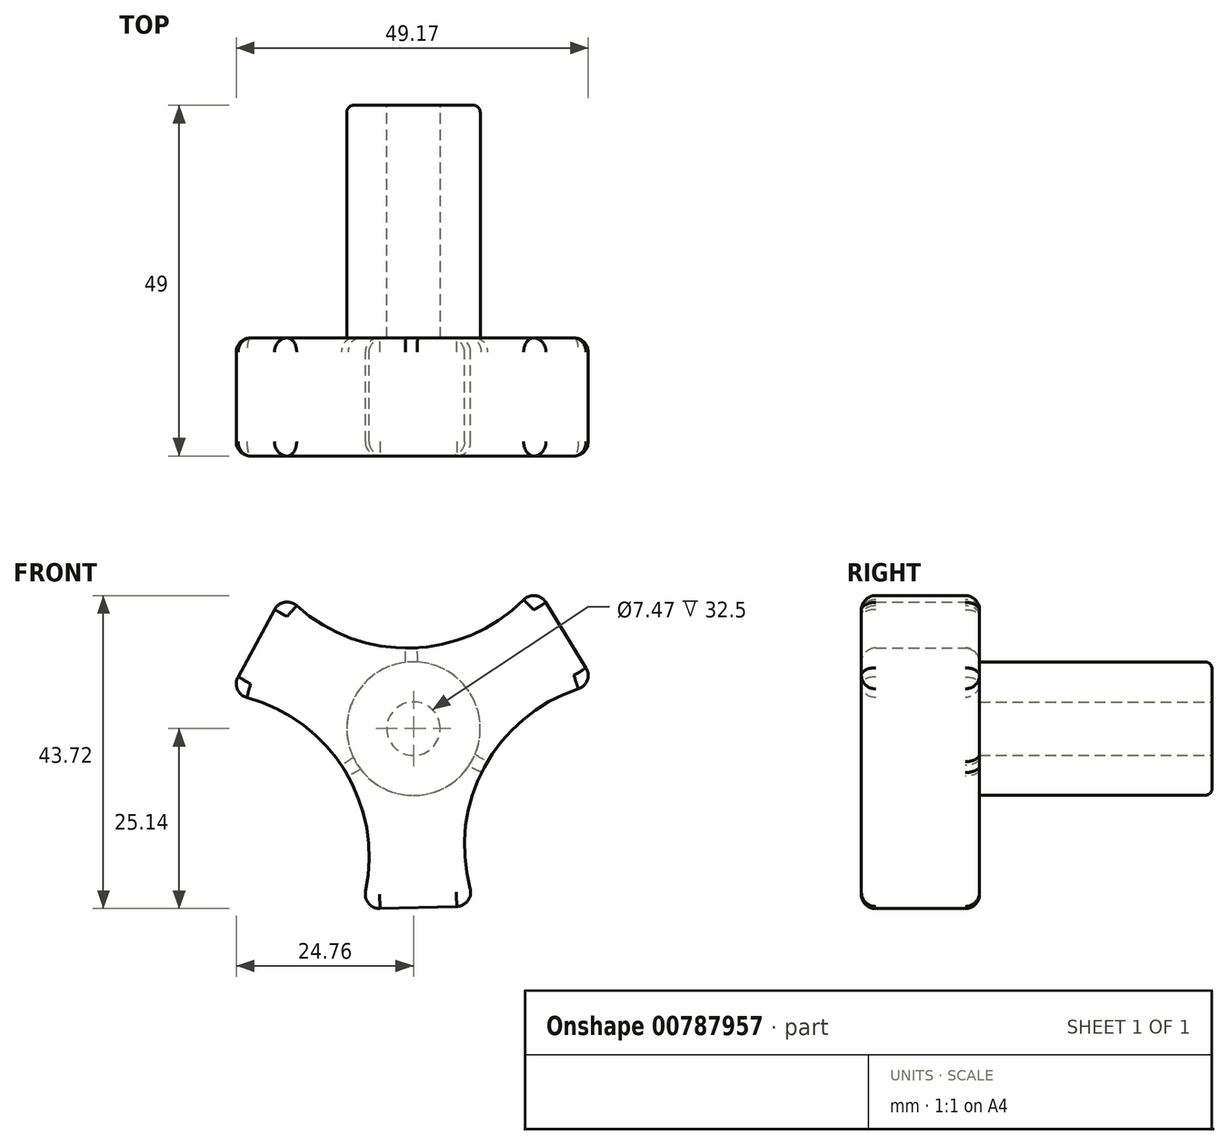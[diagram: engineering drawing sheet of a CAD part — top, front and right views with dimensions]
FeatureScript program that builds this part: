
annotation { "Feature Type Name" : "Feature", "Feature Type Description" : "" }
export const myFeature = defineFeature(function(context is Context, id is Id, definition is map)
    precondition{}
    {
        {
            var Q0;
            Q0=qCreatedBy(makeId("Front.planeOp"),FACE);
            var sketch = newSketch(context, id + "F0", { "sketchPlane" : qUnion([Q0])});
            skCircle(sketch, "E0", {"center": v(0, 0) * mm, "radius": 3.74 * mm});
            skCircle(sketch, "E1", {"center": v(0, 0) * mm, "radius": 9.33 * mm});
            skSolve(sketch);
        }
        {
            var Q0;
            Q0 = qSketchRegion(id + "F0", true);
            extrude(context, id + "F1", {"entities" : qUnion([Q0]), "depth" : 32.5 * mm, "offsetDistance" : 25 * mm});
        }
        {
            var Q0;
            Q0=makeQuery(id+"F1.opExtrude","CAP_FACE",FACE,{"disambiguationData":[OSD([sQuery(id+"F0.wireOp",EDGE,"E0"),sQuery(id+"F0.wireOp",EDGE,"E1")])],"isStart":false});
            var sketch = newSketch(context, id + "F2", { "sketchPlane" : qUnion([Q0])});
            skLineSegment(sketch, "E2", {"start": v(-21.98, 11.91) * mm, "end": v(-18.14, 19) * mm});
            skLineSegment(sketch, "E3", {"start": v(-21.98, 11.91) * mm, "end": v(-25.8, 4.87) * mm});
            skLineSegment(sketch, "E4", {"start": v(21.3, 13.08) * mm, "end": v(25.52, 6.2) * mm});
            skLineSegment(sketch, "E5", {"start": v(21.3, 13.08) * mm, "end": v(17.11, 19.91) * mm});
            skLineSegment(sketch, "E6", {"start": v(0.67, -25) * mm, "end": v(-7.37, -25.2) * mm});
            skLineSegment(sketch, "E7", {"start": v(0.67, -25) * mm, "end": v(8.73, -24.77) * mm});
            skArc(sketch, "E8", {"start": v(25.52, 6.2) * mm, "mid": v(9.9, -5.37) * mm, "end": v(8.73, -24.77) * mm});
            skArc(sketch, "E9", {"start": v(-7.37, -25.2) * mm, "mid": v(-9.6, -5.89) * mm, "end": v(-25.8, 4.87) * mm});
            skArc(sketch, "E10", {"start": v(-18.14, 19) * mm, "mid": v(-0.3, 11.27) * mm, "end": v(17.11, 19.91) * mm});
            skSolve(sketch);
        }
        {
            var Q0;
            Q0 = qSketchRegion(id + "F2", true);
            extrude(context, id + "F3", {"entities" : qUnion([Q0]), "operationType" : NewBodyOperationType.ADD, "depth" : 16.5 * mm, "offsetDistance" : 25 * mm});
        }
        {
            var Q0;
            Q0=makeQuery(id+"F3.opExtrude","CAP_EDGE",EDGE,{"disambiguationData":[OSD([sQuery(id+"F2.wireOp",EDGE,"E8")])],"isStart":false});
            var Q1;
            Q1=makeQuery(id+"F3.opExtrude","CAP_EDGE",EDGE,{"disambiguationData":[OSD([sQuery(id+"F2.wireOp",EDGE,"E9")])],"isStart":false});
            var Q2;
            Q2=makeQuery(id+"F3.opExtrude","CAP_EDGE",EDGE,{"disambiguationData":[OSD([sQuery(id+"F2.wireOp",EDGE,"E10")])],"isStart":false});
            var Q3;
            Q3=makeQuery(id+"F3.opExtrude","CAP_EDGE",EDGE,{"disambiguationData":[OSD([sQuery(id+"F2.wireOp",EDGE,"E10")])],"isStart":true});
            var Q4;
            Q4=makeQuery(id+"F3.opExtrude","CAP_EDGE",EDGE,{"disambiguationData":[OSD([sQuery(id+"F2.wireOp",EDGE,"E8")])],"isStart":true});
            var Q5;
            Q5=makeQuery(id+"F3.opExtrude","CAP_EDGE",EDGE,{"disambiguationData":[OSD([sQuery(id+"F2.wireOp",EDGE,"E9")])],"isStart":true});
            var Q6;
            Q6=makeQuery(id+"F3.opExtrude","CAP_EDGE",EDGE,{"disambiguationData":[OSD([sQuery(id+"F2.wireOp",EDGE,"E6"),sQuery(id+"F2.wireOp",EDGE,"E7")])],"isStart":true});
            var Q7;
            Q7=makeQuery(id+"F3.opExtrude","CAP_EDGE",EDGE,{"disambiguationData":[OSD([sQuery(id+"F2.wireOp",EDGE,"E6"),sQuery(id+"F2.wireOp",EDGE,"E7")])],"isStart":false});
            var Q8;
            Q8=makeQuery(id+"F3.opExtrude","CAP_EDGE",EDGE,{"disambiguationData":[OSD([sQuery(id+"F2.wireOp",EDGE,"E4"),sQuery(id+"F2.wireOp",EDGE,"E5")])],"isStart":false});
            var Q9;
            Q9=makeQuery(id+"F3.opExtrude","CAP_EDGE",EDGE,{"disambiguationData":[OSD([sQuery(id+"F2.wireOp",EDGE,"E2"),sQuery(id+"F2.wireOp",EDGE,"E3")])],"isStart":false});
            var Q10;
            Q10=makeQuery(id+"F3.opExtrude","CAP_EDGE",EDGE,{"disambiguationData":[OSD([sQuery(id+"F2.wireOp",EDGE,"E2"),sQuery(id+"F2.wireOp",EDGE,"E3")])],"isStart":true});
            var Q11;
            Q11=makeQuery(id+"F3.opExtrude","CAP_EDGE",EDGE,{"disambiguationData":[OSD([sQuery(id+"F2.wireOp",EDGE,"E4"),sQuery(id+"F2.wireOp",EDGE,"E5")])],"isStart":true});
            fillet(context, id + "F4", {"entities" : qUnion([Q0, Q1, Q2, Q3, Q4, Q5, Q6, Q7, Q8, Q9, Q10, Q11]), "radius" : 2 * mm, "tangentPropagation" : true, "allowEdgeOverflow" : false});
        }
        {
            var Q0;
            Q0=makeQuery(id+"F3.opExtrude","SWEPT_EDGE",EDGE,{"disambiguationData":[OSD([sQuery(id+"F2.wireOp",EDGE,"E4"),sQuery(id+"F2.wireOp",EDGE,"E8")])]});
            var Q1;
            Q1=makeQuery(id+"F3.opExtrude","SWEPT_EDGE",EDGE,{"disambiguationData":[OSD([sQuery(id+"F2.wireOp",EDGE,"E5"),sQuery(id+"F2.wireOp",EDGE,"E10")])]});
            var Q2;
            Q2=makeQuery(id+"F3.opExtrude","SWEPT_EDGE",EDGE,{"disambiguationData":[OSD([sQuery(id+"F2.wireOp",EDGE,"E2"),sQuery(id+"F2.wireOp",EDGE,"E10")])]});
            var Q3;
            Q3=makeQuery(id+"F3.opExtrude","SWEPT_EDGE",EDGE,{"disambiguationData":[OSD([sQuery(id+"F2.wireOp",EDGE,"E3"),sQuery(id+"F2.wireOp",EDGE,"E9")])]});
            var Q4;
            Q4=makeQuery(id+"F3.opExtrude","SWEPT_EDGE",EDGE,{"disambiguationData":[OSD([sQuery(id+"F2.wireOp",EDGE,"E6"),sQuery(id+"F2.wireOp",EDGE,"E9")])]});
            var Q5;
            Q5=makeQuery(id+"F3.opExtrude","SWEPT_EDGE",EDGE,{"disambiguationData":[OSD([sQuery(id+"F2.wireOp",EDGE,"E7"),sQuery(id+"F2.wireOp",EDGE,"E8")])]});
            fillet(context, id + "F5", {"entities" : qUnion([Q0, Q1, Q2, Q3, Q4, Q5]), "radius" : 2 * mm, "tangentPropagation" : true, "allowEdgeOverflow" : false});
        }
        {
            var Q0;
            Q0=makeQuery(id+"F1.opExtrude","CAP_EDGE",EDGE,{"disambiguationData":[OSD([sQuery(id+"F0.wireOp",EDGE,"E1")])],"isStart":true});
            fillet(context, id + "F6", {"entities" : qUnion([Q0]), "radius" : 1 * mm, "tangentPropagation" : true, "allowEdgeOverflow" : false});
        }
    });
